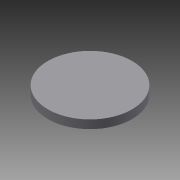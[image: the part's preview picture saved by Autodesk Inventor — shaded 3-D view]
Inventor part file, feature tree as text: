
AUTODESK INVENTOR PART (.ipt)
format: ipt  version: 2015 (Build 190159000, 159)  size: 68,096 bytes
history: native  units: in
note: dims shown in document units (in); Inventor stores cm internally (conversion verified against a paired STEP export)
features: extrude x1, sketch x1
ambient origin geometry x8: Origin, YZ Plane, XZ Plane, XY Plane, X Axis, Y Axis, Z Axis, Center Point
bodies: Solid1 (feature_tree)
feature tree (2):
  extrude  "Extrusion1"  Depth=0.3937in TaperAngle=0.0deg
  sketch  "Sketch1"  dims[d0=3.937in d1=0.3937in d2=0.0in]
